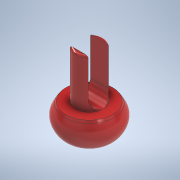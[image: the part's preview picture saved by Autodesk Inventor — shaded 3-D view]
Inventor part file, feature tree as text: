
AUTODESK INVENTOR PART (.ipt)
format: ipt  version: 2022 (Build 260153000, 153)  size: 198,144 bytes
history: native  units: mm
features: extrude x3, sketch x3, fillet x2, chamfer x1
ambient origin geometry x8: Origin, YZ Plane, XZ Plane, XY Plane, X Axis, Y Axis, Z Axis, Center Point
bodies: Solid1 (feature_tree)
feature tree (9):
  extrude  "Extrusion1"  Depth=3.0mm
  chamfer  "Chamfer1"  Distance=3.0mm
  extrude  "Extrusion2"  Depth=3.0mm
  fillet  "Fillet1"  Radius=5.0mm
  fillet  "Fillet2"  Radius=0.2mm
  extrude  "Extrusion3"  Depth=2.1mm
  sketch  "Sketch1"  dims[d0=4.8mm d1=8.8mm d2=3.0mm d3=0.0mm]
  sketch  "Sketch2"  dims[d4=2.0mm d5=3.0mm d6=45.0deg d7=2.8mm d8=5.0mm d9=0.0mm d10=0.2mm]
  sketch  "Sketch3"  dims[d11=1.8mm d12=2.1mm d13=0.0mm d14=0.0mm]
